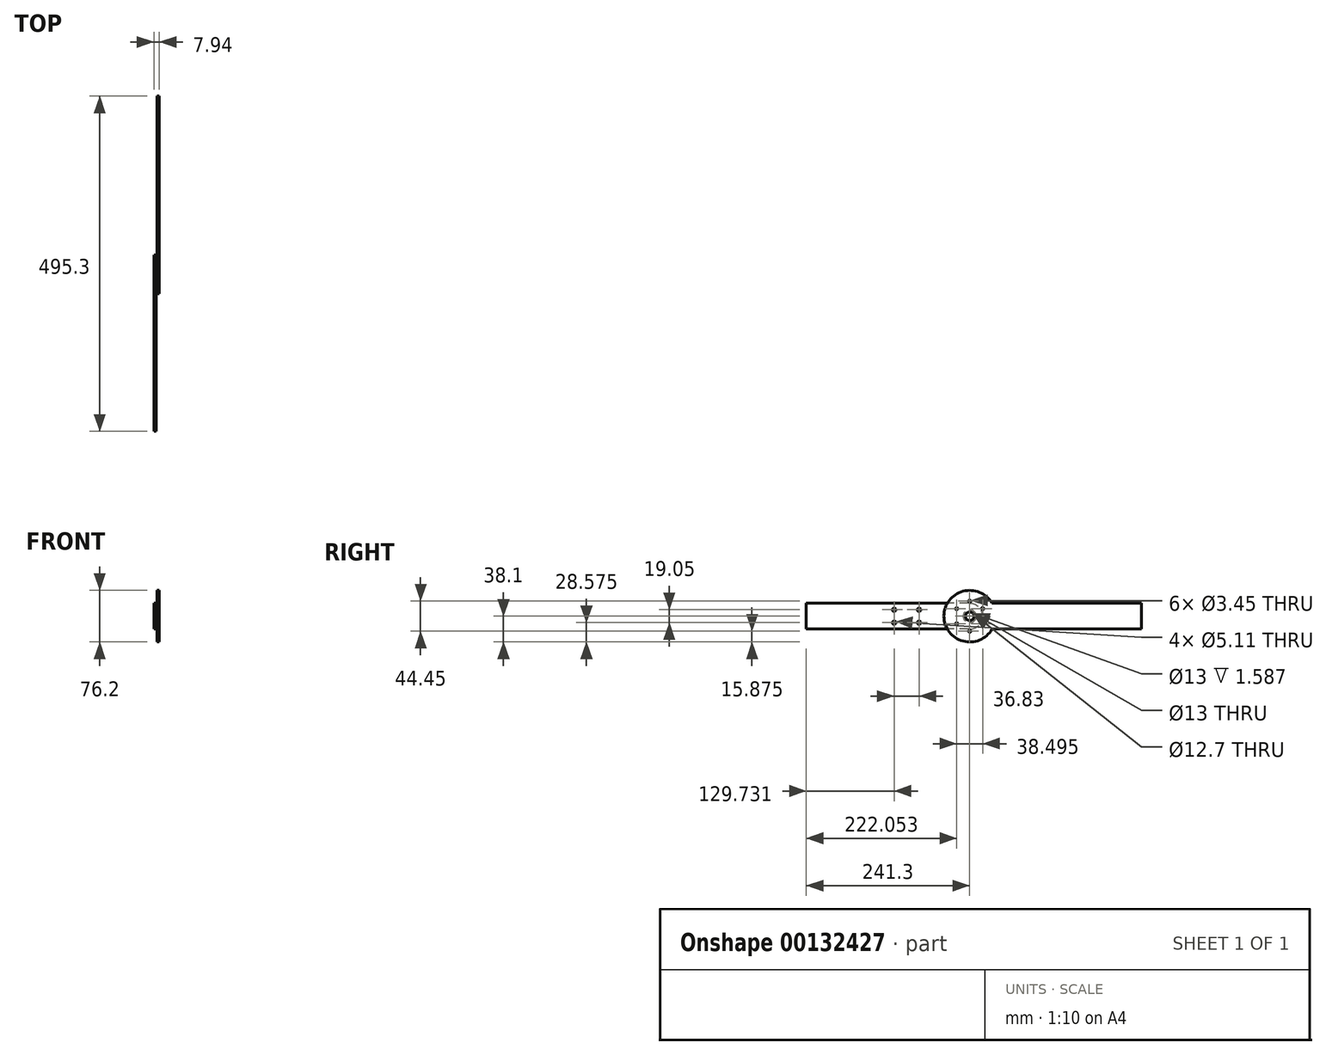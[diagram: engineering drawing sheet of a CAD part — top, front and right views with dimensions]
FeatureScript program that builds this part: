
annotation { "Feature Type Name" : "Feature", "Feature Type Description" : "" }
export const myFeature = defineFeature(function(context is Context, id is Id, definition is map)
    precondition{}
    {
        {
            var Q0;
            Q0=qCreatedBy(makeId("Right.planeOp"),FACE);
            var sketch = newSketch(context, id + "F0", { "sketchPlane" : qUnion([Q0])});
            skCircle(sketch, "E0", {"center": v(0, 0) * mm, "radius": 38.1 * mm});
            skLineSegment(sketch, "E1.bottom", {"start": v(35.92, -12.7) * mm, "end": v(254, -12.7) * mm});
            skLineSegment(sketch, "E1.top", {"start": v(35.92, 12.7) * mm, "end": v(254, 12.7) * mm});
            skLineSegment(sketch, "E1.left", {"start": v(35.92, -12.7) * mm, "end": v(35.92, 12.7) * mm});
            skLineSegment(sketch, "E1.right", {"start": v(254, -12.7) * mm, "end": v(254, 12.7) * mm});
            skCircle(sketch, "E2", {"center": v(0, 0) * mm, "radius": 6.35 * mm});
            skSolve(sketch);
        }
        {
            var Q0;
            {var subQ0=sQuery(id+"F0.wireOp",EDGE,"E1.left");Q0=makeQuery(id+"F0.imprint","IMPRINT",FACE,{"disambiguationData":[TD([[makeQuery(id+"F0.imprint","IMPRINT",EDGE,{"derivedFrom":subQ0}),1.0]])]});}
            var Q1;
            {var subQ1=sQuery(id+"F0.wireOp",EDGE,"E1.bottom");Q1=makeQuery(id+"F0.imprint","IMPRINT",FACE,{"disambiguationData":[TD([[makeQuery(id+"F0.imprint","IMPRINT",EDGE,{"derivedFrom":subQ1}),1.0]])]});}
            var Q2;
            {var subQ0=sQuery(id+"F0.wireOp",EDGE,"E1.left");Q2=makeQuery(id+"F0.imprint","IMPRINT",FACE,{"disambiguationData":[TD([[makeQuery(id+"F0.imprint","IMPRINT",EDGE,{"derivedFrom":subQ0}),-1.0]])]});}
            extrude(context, id + "F1", {"entities" : qUnion([Q0, Q1, Q2]), "depth" : 3.17 * mm});
        }
        {
            var Q0;
            Q0=makeQuery(id+"F1.opExtrude","CAP_FACE",FACE,{"disambiguationData":[OSD([sQuery(id+"F0.wireOp",EDGE,"E0"),sQuery(id+"F0.wireOp",EDGE,"E1.bottom"),sQuery(id+"F0.wireOp",EDGE,"E1.top"),sQuery(id+"F0.wireOp",EDGE,"E1.right"),sQuery(id+"F0.wireOp",EDGE,"E2")])],"isStart":true});
            var sketch = newSketch(context, id + "F2", { "sketchPlane" : qUnion([Q0])});
            skCircle(sketch, "E3", {"center": v(0, 0) * mm, "radius": 9.53 * mm});
            skCircle(sketch, "E4", {"center": v(0, 0) * mm, "radius": 6.5 * mm});
            skSolve(sketch);
        }
        {
            var Q0;
            Q0 = qSketchRegion(id + "F2", true);
            extrude(context, id + "F3", {"entities" : qUnion([Q0]), "depth" : 1.59 * mm});
        }
        {
            var Q0;
            Q0=makeQuery(id+"F1.opExtrude","CAP_FACE",FACE,{"disambiguationData":[OSD([sQuery(id+"F0.wireOp",EDGE,"E0"),sQuery(id+"F0.wireOp",EDGE,"E1.bottom"),sQuery(id+"F0.wireOp",EDGE,"E1.top"),sQuery(id+"F0.wireOp",EDGE,"E1.right"),sQuery(id+"F0.wireOp",EDGE,"E2")])],"isStart":false});
            var sketch = newSketch(context, id + "F4", { "sketchPlane" : qUnion([Q0])});
            skArc(sketch, "E5.0.0", {"start": v(35.92, 12.7) * mm, "mid": v(-38.1, 0) * mm, "end": v(35.92, -12.7) * mm});
            skLineSegment(sketch, "E5.0.1", {"start": v(35.92, -12.7) * mm, "end": v(254, -12.7) * mm});
            skLineSegment(sketch, "E5.0.2", {"start": v(254, -12.7) * mm, "end": v(254, 12.7) * mm});
            skLineSegment(sketch, "E5.0.3", {"start": v(254, 12.7) * mm, "end": v(35.92, 12.7) * mm});
            skCircle(sketch, "E6", {"center": v(0, 0) * mm, "radius": 22.23 * mm, "construction": true});
            skPoint(sketch, "E7", {"position": v(0, 22.23) * mm});
            skPoint(sketch, "E8.1.0", {"position": v(-19.25, 11.11) * mm});
            skPoint(sketch, "E8.2.0", {"position": v(-19.25, -11.11) * mm});
            skPoint(sketch, "E9.0.3.0", {"position": v(0, -22.23) * mm});
            skPoint(sketch, "E10.0.4.0", {"position": v(19.25, -11.11) * mm});
            skPoint(sketch, "E10.0.5.0", {"position": v(19.25, 11.11) * mm});
            skSolve(sketch);
        }
        {
            var Q0;
            Q0=sQuery(id+"F4.wireOp",VERTEX,"E7");
            var Q1;
            Q1=sQuery(id+"F4.wireOp",VERTEX,"E8.2.0");
            var Q2;
            Q2=sQuery(id+"F4.wireOp",VERTEX,"E8.1.0");
            var Q3;
            Q3=sQuery(id+"F4.wireOp",VERTEX,"E9.0.3.0");
            var Q4;
            Q4=sQuery(id+"F4.wireOp",VERTEX,"E10.0.5.0");
            var Q5;
            Q5=sQuery(id+"F4.wireOp",VERTEX,"E10.0.4.0");
            var Q6;
            Q6=makeQuery(id+"F1.opExtrude","SWEPT_BODY",BODY,{"disambiguationData":[OSD([sQuery(id+"F0.wireOp",EDGE,"E0"),sQuery(id+"F0.wireOp",EDGE,"E1.bottom"),sQuery(id+"F0.wireOp",EDGE,"E1.top"),sQuery(id+"F0.wireOp",EDGE,"E1.right"),sQuery(id+"F0.wireOp",EDGE,"E2")])]});
            hole(context, id + "F5", {"style" : HoleStyle.SIMPLE, "endStyle" : HoleEndStyle.THROUGH, "standardTappedOrClearance" : lookupTablePath({ "standard" : "ANSI", "engagement" : "75%", "pitch" : "32 tpi", "size" : "#8", "type" : "Tapped" }), "standardBlindInLast" : lookupTablePath({ "standard" : "ANSI", "engagement" : "75%", "pitch" : "32 tpi", "size" : "#8", "type" : "Tapped" }), "holeDiameter" : 3.45 * mm, "locations" : qUnion([Q0, Q1, Q2, Q3, Q4, Q5]), "scope" : qUnion([Q6]), "isTappedThrough" : true, "majorDiameter" : 4.17 * mm, "showTappedDepth" : true});
        }
        {
            var Q0;
            Q0=makeQuery(id+"F3.opExtrude","CAP_FACE",FACE,{"disambiguationData":[OSD([sQuery(id+"F2.wireOp",EDGE,"E3"),sQuery(id+"F2.wireOp",EDGE,"E4")])],"isStart":false});
            var sketch = newSketch(context, id + "F6", { "sketchPlane" : qUnion([Q0])});
            skLineSegment(sketch, "E11.bottom", {"start": v(0, 19.05) * mm, "end": v(241.3, 19.05) * mm});
            skLineSegment(sketch, "E11.top", {"start": v(0, -19.05) * mm, "end": v(241.3, -19.05) * mm});
            skLineSegment(sketch, "E11.left", {"start": v(-19.05, 0) * mm, "end": v(-19.05, 0) * mm});
            skLineSegment(sketch, "E11.right", {"start": v(241.3, 19.05) * mm, "end": v(241.3, -19.05) * mm});
            skPoint(sketch, "E12.visualSharp", {"position": v(-19.05, 19.05) * mm});
            skArc(sketch, "E12.filletArc", {"start": v(0, 19.05) * mm, "mid": v(-13.47, 13.47) * mm, "end": v(-19.05, 0) * mm});
            skPoint(sketch, "E13.visualSharp", {"position": v(-19.05, -19.05) * mm});
            skArc(sketch, "E13.filletArc", {"start": v(-19.05, 0) * mm, "mid": v(-13.47, -13.47) * mm, "end": v(0, -19.05) * mm});
            skCircle(sketch, "E14", {"center": v(0, 0) * mm, "radius": 6.35 * mm});
            skPoint(sketch, "E15", {"position": v(74.74, 9.52) * mm});
            skPoint(sketch, "E16", {"position": v(74.74, -9.53) * mm});
            skPoint(sketch, "E17", {"position": v(111.57, -9.53) * mm});
            skPoint(sketch, "E18", {"position": v(111.57, 9.52) * mm});
            skLineSegment(sketch, "E19", {"start": v(115.38, 19.05) * mm, "end": v(115.38, -19.05) * mm, "construction": true});
            skSolve(sketch);
        }
        {
            var Q0;
            Q0=makeQuery(id+"F6.imprint","IMPRINT",FACE,{"disambiguationData":[TD([[makeQuery(id+"F6.imprint","IMPRINT",EDGE,{"derivedFrom":sQuery(id+"F6.wireOp",EDGE,"E11.bottom")}),-1.0]])]});
            var Q1;
            Q1=makeQuery(id+"F6.imprint","IMPRINT",FACE,{"disambiguationData":[TD([[makeQuery(id+"F6.imprint","IMPRINT",EDGE,{"derivedFrom":makeQuery(id+"F3.opExtrude","CAP_EDGE",EDGE,{"disambiguationData":[OSD([sQuery(id+"F2.wireOp",EDGE,"E3")])],"isStart":false})}),1.0]])]});
            extrude(context, id + "F7", {"entities" : qUnion([Q0, Q1]), "depth" : 3.17 * mm});
        }
        {
            var Q0;
            Q0=sQuery(id+"F6.wireOp",VERTEX,"E18");
            var Q1;
            Q1=sQuery(id+"F6.wireOp",VERTEX,"E15");
            var Q2;
            Q2=sQuery(id+"F6.wireOp",VERTEX,"E16");
            var Q3;
            Q3=sQuery(id+"F6.wireOp",VERTEX,"E17");
            var Q4;
            Q4=makeQuery(id+"F7.opExtrude","SWEPT_BODY",BODY,{"disambiguationData":[OSD([sQuery(id+"F2.wireOp",EDGE,"E4"),sQuery(id+"F6.wireOp",EDGE,"E11.bottom"),sQuery(id+"F6.wireOp",EDGE,"E11.top"),sQuery(id+"F6.wireOp",EDGE,"E11.right"),sQuery(id+"F6.wireOp",EDGE,"E12.filletArc"),sQuery(id+"F6.wireOp",EDGE,"E13.filletArc")])]});
            hole(context, id + "F8", {"style" : HoleStyle.SIMPLE, "endStyle" : HoleEndStyle.THROUGH, "oppositeDirection" : true, "standardTappedOrClearance" : lookupTablePath({ "standard" : "ANSI", "fit" : "Normal (ASME)", "size" : "#10", "type" : "Clearance" }), "standardBlindInLast" : lookupTablePath({ "fit" : "Free", "standard" : "ANSI", "size" : "#10", "type" : "Clearance" }), "holeDiameter" : 5.1 * mm, "locations" : qUnion([Q0, Q1, Q2, Q3]), "scope" : qUnion([Q4]), "isTappedThrough" : true});
        }
        {
            var Q0;
            Q0=makeQuery(id+"F1.opExtrude","CAP_FACE",FACE,{"disambiguationData":[OSD([sQuery(id+"F0.wireOp",EDGE,"E0"),sQuery(id+"F0.wireOp",EDGE,"E1.bottom"),sQuery(id+"F0.wireOp",EDGE,"E1.top"),sQuery(id+"F0.wireOp",EDGE,"E1.right"),sQuery(id+"F0.wireOp",EDGE,"E2")])],"isStart":true});
            var sketch = newSketch(context, id + "F9", { "sketchPlane" : qUnion([Q0])});
            skLineSegment(sketch, "E20", {"start": v(-254, 12.7) * mm, "end": v(-254, 19.05) * mm});
            skLineSegment(sketch, "E21", {"start": v(-254, 19.05) * mm, "end": v(-33, 19.05) * mm});
            skLineSegment(sketch, "E22.0", {"start": v(-35.92, 12.7) * mm, "end": v(-254, 12.7) * mm});
            skArc(sketch, "E23.0", {"start": v(-35.92, 12.7) * mm, "mid": v(-34.6, 15.94) * mm, "end": v(-33, 19.05) * mm});
            skPoint(sketch, "E24.orphan", {"position": v(-35.92, -12.7) * mm});
            skLineSegment(sketch, "E25", {"start": v(-254, -12.7) * mm, "end": v(-254, -19.05) * mm});
            skLineSegment(sketch, "E26", {"start": v(-254, -19.05) * mm, "end": v(-33, -19.05) * mm});
            skLineSegment(sketch, "E27.0", {"start": v(-35.92, -12.7) * mm, "end": v(-254, -12.7) * mm});
            skSolve(sketch);
        }
        {
            var Q0;
            Q0=makeQuery(id+"F9.imprint","IMPRINT",FACE,{"disambiguationData":[TD([[makeQuery(id+"F9.imprint","IMPRINT",EDGE,{"derivedFrom":sQuery(id+"F9.wireOp",EDGE,"E20")}),-1.0]])]});
            var Q1;
            Q1=makeQuery(id+"F9.imprint","IMPRINT",FACE,{"disambiguationData":[TD([[makeQuery(id+"F9.imprint","IMPRINT",EDGE,{"derivedFrom":sQuery(id+"F9.wireOp",EDGE,"E25")}),1.0]])]});
            extrude(context, id + "F10", {"entities" : qUnion([Q0, Q1]), "operationType" : NewBodyOperationType.ADD, "oppositeDirection" : true, "depth" : 3.17 * mm});
        }
    });
